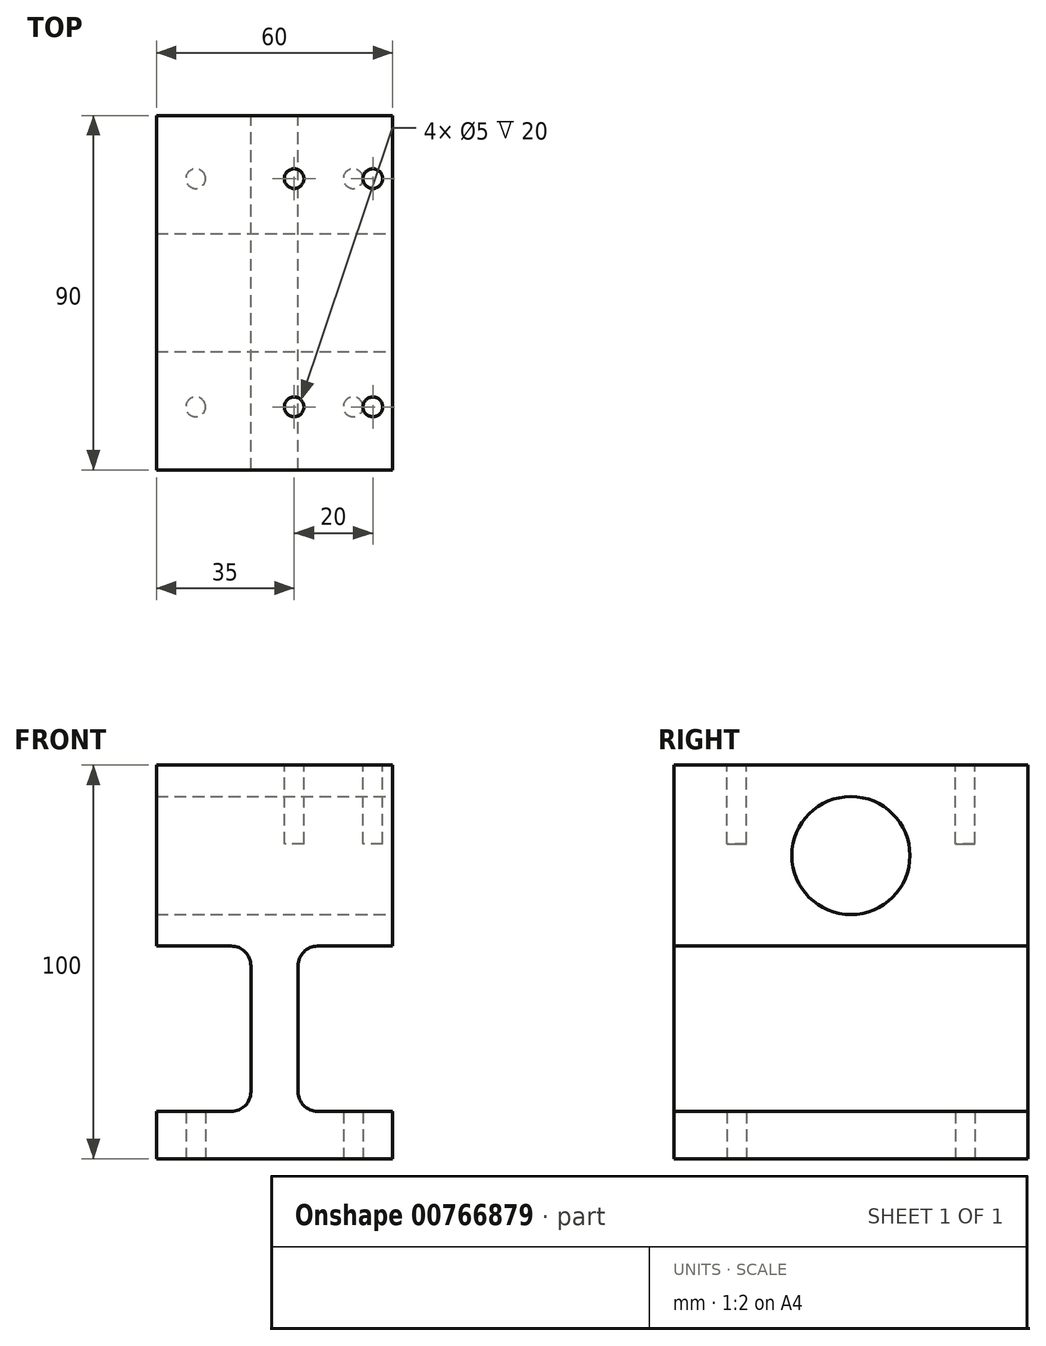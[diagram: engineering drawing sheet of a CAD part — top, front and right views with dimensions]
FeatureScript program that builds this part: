
annotation { "Feature Type Name" : "Feature", "Feature Type Description" : "" }
export const myFeature = defineFeature(function(context is Context, id is Id, definition is map)
    precondition{}
    {
        {
            var Q0;
            Q0=qCreatedBy(makeId("Front.planeOp"),FACE);
            var sketch = newSketch(context, id + "F0", { "sketchPlane" : qUnion([Q0])});
            skLineSegment(sketch, "E0", {"start": v(0, 0) * mm, "end": v(60, 0) * mm});
            skLineSegment(sketch, "E1", {"start": v(60, 0) * mm, "end": v(60, 12) * mm});
            skLineSegment(sketch, "E2", {"start": v(60, 12) * mm, "end": v(36, 12) * mm});
            skLineSegment(sketch, "E3", {"start": v(36, 12) * mm, "end": v(36, 54) * mm});
            skLineSegment(sketch, "E4", {"start": v(36, 54) * mm, "end": v(60, 54) * mm});
            skLineSegment(sketch, "E5", {"start": v(60, 54) * mm, "end": v(60, 100) * mm});
            skLineSegment(sketch, "E6", {"start": v(60, 100) * mm, "end": v(0, 100) * mm});
            skLineSegment(sketch, "E7", {"start": v(0, 100) * mm, "end": v(0, 54) * mm});
            skLineSegment(sketch, "E8", {"start": v(0, 54) * mm, "end": v(24, 54) * mm});
            skLineSegment(sketch, "E9", {"start": v(24, 54) * mm, "end": v(24, 12) * mm});
            skLineSegment(sketch, "E10", {"start": v(24, 12) * mm, "end": v(0, 12) * mm});
            skLineSegment(sketch, "E11", {"start": v(0, 12) * mm, "end": v(0, 0) * mm});
            skSolve(sketch);
        }
        {
            var Q0;
            Q0=makeQuery(id+"F0.imprint","IMPRINT",FACE,{"disambiguationData":[TD([[makeQuery(id+"F0.imprint","IMPRINT",EDGE,{"derivedFrom":sQuery(id+"F0.wireOp",EDGE,"E0")}),1.0]])]});
            extrude(context, id + "F1", {"entities" : qUnion([Q0]), "depth" : 45 * mm, "offsetDistance" : 25 * mm, "hasSecondDirection" : true, "secondDirectionOppositeDirection" : true, "secondDirectionDepth" : 45 * mm});
        }
        {
            var Q0;
            Q0=makeQuery(id+"F1.opExtrude","SWEPT_EDGE",EDGE,{"disambiguationData":[OSD([sQuery(id+"F0.wireOp",EDGE,"E3"),sQuery(id+"F0.wireOp",EDGE,"E4")])]});
            var Q1;
            Q1=makeQuery(id+"F1.opExtrude","SWEPT_EDGE",EDGE,{"disambiguationData":[OSD([sQuery(id+"F0.wireOp",EDGE,"E2"),sQuery(id+"F0.wireOp",EDGE,"E3")])]});
            var Q2;
            Q2=makeQuery(id+"F1.opExtrude","SWEPT_EDGE",EDGE,{"disambiguationData":[OSD([sQuery(id+"F0.wireOp",EDGE,"E9"),sQuery(id+"F0.wireOp",EDGE,"E10")])]});
            var Q3;
            Q3=makeQuery(id+"F1.opExtrude","SWEPT_EDGE",EDGE,{"disambiguationData":[OSD([sQuery(id+"F0.wireOp",EDGE,"E8"),sQuery(id+"F0.wireOp",EDGE,"E9")])]});
            fillet(context, id + "F2", {"entities" : qUnion([Q0, Q1, Q2, Q3]), "radius" : 5 * mm, "tangentPropagation" : true, "allowEdgeOverflow" : false});
        }
        {
            var Q0;
            Q0=makeQuery(id+"F1.opExtrude","SWEPT_FACE",FACE,{"disambiguationData":[OSD([sQuery(id+"F0.wireOp",EDGE,"E5")])]});
            var sketch = newSketch(context, id + "F3", { "sketchPlane" : qUnion([Q0])});
            skCircle(sketch, "E12", {"center": v(0, 141.56) * mm, "radius": 15 * mm});
            skCircle(sketch, "E13", {"center": v(0, 77) * mm, "radius": 15 * mm});
            skSolve(sketch);
        }
        {
            var Q0;
            Q0=makeQuery(id+"F3.imprint","IMPRINT",FACE,{"disambiguationData":[TD([[makeQuery(id+"F3.imprint","IMPRINT",EDGE,{"derivedFrom":sQuery(id+"F3.wireOp",EDGE,"E13")}),1.0]])]});
            extrude(context, id + "F4", {"entities" : qUnion([Q0]), "operationType" : NewBodyOperationType.REMOVE, "oppositeDirection" : true, "depth" : 60 * mm, "offsetDistance" : 25 * mm});
        }
        {
            var Q0;
            Q0=makeQuery(id+"F1.opExtrude","SWEPT_FACE",FACE,{"disambiguationData":[OSD([sQuery(id+"F0.wireOp",EDGE,"E0")])]});
            var sketch = newSketch(context, id + "F5", { "sketchPlane" : qUnion([Q0])});
            skCircle(sketch, "E14", {"center": v(10, 29) * mm, "radius": 2.5 * mm});
            skCircle(sketch, "E15", {"center": v(50, 29) * mm, "radius": 2.5 * mm});
            skCircle(sketch, "E16", {"center": v(50, -29) * mm, "radius": 2.5 * mm});
            skCircle(sketch, "E17", {"center": v(10, -29) * mm, "radius": 2.5 * mm});
            skSolve(sketch);
        }
        {
            var Q0;
            Q0=makeQuery(id+"F5.imprint","IMPRINT",FACE,{"disambiguationData":[TD([[makeQuery(id+"F5.imprint","IMPRINT",EDGE,{"derivedFrom":sQuery(id+"F5.wireOp",EDGE,"E14")}),1.0]])]});
            var Q1;
            Q1=makeQuery(id+"F5.imprint","IMPRINT",FACE,{"disambiguationData":[TD([[makeQuery(id+"F5.imprint","IMPRINT",EDGE,{"derivedFrom":sQuery(id+"F5.wireOp",EDGE,"E17")}),1.0]])]});
            var Q2;
            Q2=makeQuery(id+"F5.imprint","IMPRINT",FACE,{"disambiguationData":[TD([[makeQuery(id+"F5.imprint","IMPRINT",EDGE,{"derivedFrom":sQuery(id+"F5.wireOp",EDGE,"E16")}),1.0]])]});
            var Q3;
            Q3=makeQuery(id+"F5.imprint","IMPRINT",FACE,{"disambiguationData":[TD([[makeQuery(id+"F5.imprint","IMPRINT",EDGE,{"derivedFrom":sQuery(id+"F5.wireOp",EDGE,"E15")}),1.0]])]});
            extrude(context, id + "F6", {"entities" : qUnion([Q0, Q1, Q2, Q3]), "operationType" : NewBodyOperationType.REMOVE, "oppositeDirection" : true, "depth" : 12 * mm, "offsetDistance" : 25 * mm});
        }
        {
            var Q0;
            Q0=makeQuery(id+"F1.opExtrude","SWEPT_FACE",FACE,{"disambiguationData":[OSD([sQuery(id+"F0.wireOp",EDGE,"E6")])]});
            var sketch = newSketch(context, id + "F7", { "sketchPlane" : qUnion([Q0])});
            skCircle(sketch, "E18", {"center": v(55, 29) * mm, "radius": 2.5 * mm});
            skCircle(sketch, "E19", {"center": v(35, 29) * mm, "radius": 2.5 * mm});
            skCircle(sketch, "E20", {"center": v(35, -29) * mm, "radius": 2.5 * mm});
            skCircle(sketch, "E21", {"center": v(55, -29) * mm, "radius": 2.5 * mm});
            skSolve(sketch);
        }
        {
            var Q0;
            Q0=makeQuery(id+"F7.imprint","IMPRINT",FACE,{"disambiguationData":[TD([[makeQuery(id+"F7.imprint","IMPRINT",EDGE,{"derivedFrom":sQuery(id+"F7.wireOp",EDGE,"E19")}),1.0]])]});
            var Q1;
            Q1=makeQuery(id+"F7.imprint","IMPRINT",FACE,{"disambiguationData":[TD([[makeQuery(id+"F7.imprint","IMPRINT",EDGE,{"derivedFrom":sQuery(id+"F7.wireOp",EDGE,"E18")}),1.0]])]});
            var Q2;
            Q2=makeQuery(id+"F7.imprint","IMPRINT",FACE,{"disambiguationData":[TD([[makeQuery(id+"F7.imprint","IMPRINT",EDGE,{"derivedFrom":sQuery(id+"F7.wireOp",EDGE,"E21")}),1.0]])]});
            var Q3;
            Q3=makeQuery(id+"F7.imprint","IMPRINT",FACE,{"disambiguationData":[TD([[makeQuery(id+"F7.imprint","IMPRINT",EDGE,{"derivedFrom":sQuery(id+"F7.wireOp",EDGE,"E20")}),1.0]])]});
            extrude(context, id + "F8", {"entities" : qUnion([Q0, Q1, Q2, Q3]), "operationType" : NewBodyOperationType.REMOVE, "oppositeDirection" : true, "depth" : 20 * mm, "offsetDistance" : 25 * mm});
        }
    });
